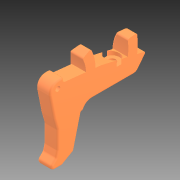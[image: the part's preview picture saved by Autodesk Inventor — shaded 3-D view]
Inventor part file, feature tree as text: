
AUTODESK INVENTOR PART (.ipt)
format: ipt  version: 2020 (Build 240168000, 168)  size: 771,584 bytes
history: native  units: in
note: dims shown in document units (in); Inventor stores cm internally (conversion verified against a paired STEP export)
features: extrude x13, sketch x13, fillet x5, plane x2, projected_geometry x2, revolve x1, chamfer x1, imported_body x1
ambient origin geometry x8: Origin, YZ Plane, XZ Plane, XY Plane, X Axis, Y Axis, Z Axis, Center Point
bodies: Solid1 (feature_tree)
feature tree (38):
  extrude  "Extrusion1"  Depth=0.3937in TaperAngle=0.0deg
  extrude  "Extrusion2"  Depth=0.5906in
  extrude  "Extrusion3"  TaperAngle=90.0deg  [1 undecoded]
  revolve  "Revolution1"  [1 undecoded]
  extrude  "Extrusion4"  TaperAngle=0.0deg  [1 undecoded]
  extrude  "Extrusion5"  Depth=0.1181in
  extrude  "Extrusion6"  TaperAngle=0.0deg  [1 undecoded]
  extrude  "Extrusion8"  TaperAngle=0.0deg  [1 undecoded]
  fillet  "Fillet2"  Radius=0.0394in
  fillet  "Fillet4"  Radius=0.0394in
  sketch  "Sketch11"  dims[d50=0.1969in d51=0.1969in]
  extrude  "Extrusion10"  Depth=0.1969in
  extrude  "Extrusion14"  Depth=2.9528in
  extrude  "Extrusion11"  Depth=0.0787in TaperAngle=0.0deg
  plane  "Work Plane3"
  plane  "Work Plane4"
  extrude  "Extrusion15"  Depth=0.0394in TaperAngle=0.0deg
  extrude  "Extrusion16"  Depth=0.3937in TaperAngle=0.0deg
  fillet  "Fillet9"  Radius=0.1378in
  fillet  "Fillet10"  Radius=0.3937in
  extrude  "Extrusion17"  Depth=0.0295in
  chamfer  "Chamfer4"  Distance=0.0394in
  fillet  "Fillet11"  Radius=0.0295in
  sketch  "Sketch1"  dims[d0=0.0in d1=0.0in d2=0.3937in d3=0.0in]
  sketch  "Sketch2"  dims[d4=0.1969in d5=0.5906in]
  sketch  "Sketch3"  dims[d6=0.0787in d7=90.0deg]
  sketch  "Sketch4"  dims[d8=0.1575in d9=0.315in]
  sketch  "Sketch5"  dims[d10=0.0787in d11=0.0in d12=0.0in d13=0.0in]
  sketch  "Sketch6"  dims[d14=0.0481in d15=0.1181in]
  sketch  "Sketch7"  dims[d16=0.7874in d17=0.0in d18=0.0in]
  sketch  "Sketch9"  dims[d19=0.0in d20=0.0in d32=0.0in d33=0.0in d34=0.0394in d36=0.0394in]
  sketch  "Sketch12"  dims[d52=1.1811in d53=2.9528in]
  projected_geometry  "Projected Loop1"
  sketch  "Sketch15"  dims[d55=0.1718in d56=15.0deg d59=0.0787in d60=0.0in]
  sketch  "Sketch16"  dims[d61=0.0295in d62=0.0in d71=0.0394in d72=0.0in]
  sketch  "Sketch17"  dims[d73=0.1378in d74=0.3937in d75=0.0in d76=0.1378in d77=0.3937in d78=0.0in d79=0.0295in d80=0.0394in d81=0.0295in d82=0.0in d83=0.4921in d84=0.3937in d85=0.0394in d86=0.0787in d87=45.0deg d88=0.0394in]
  projected_geometry  "Projected Loop2"
  imported_body  "Base1"
note: 5 required parameter values undecoded (feature->parameter linkage not recoverable at this tier; creation-order binding heuristic only, values carry confidence <= 0.55)